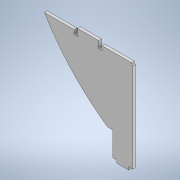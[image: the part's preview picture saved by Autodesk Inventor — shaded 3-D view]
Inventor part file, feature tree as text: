
AUTODESK INVENTOR PART (.ipt)
format: ipt  version: 2020 (Build 240168000, 168)  size: 203,776 bytes
history: native  units: mm
features: extrude x1, sketch x1
ambient origin geometry x8: Origin, YZ Plane, XZ Plane, XY Plane, X Axis, Y Axis, Z Axis, Center Point
bodies: Solid1 (feature_tree)
feature tree (2):
  extrude  "Extrusion1"  Depth=7.0mm
  sketch  "Sketch1"  dims[d13=550.0mm d17=200.0mm d18=0.0mm d54=220.0mm d56=220.0mm d57=30.0mm d59=30.0mm d62=252.393783mm d73=236.680872mm d74=236.680872mm d75=576.435mm d76=472.393783mm d77=472.393783mm d78=30.0mm d81=220.0mm d82=252.393783mm d85=356.435mm d88=3.5mm d91=3.5mm d105=2.666667mm d106=30.0mm d107=20.0mm d108=2.666667mm d109=1.333333mm d110=7.333333mm d111=7.333333mm d112=7.5mm d113=3.75mm d114=3.75mm d140=7.5mm d171=1.75mm d172=10.0mm d173=3.5mm d174=7.0mm d175=0.0mm d176=7.0mm d179=230.666667mm d182=3.5mm d183=7.0mm]
